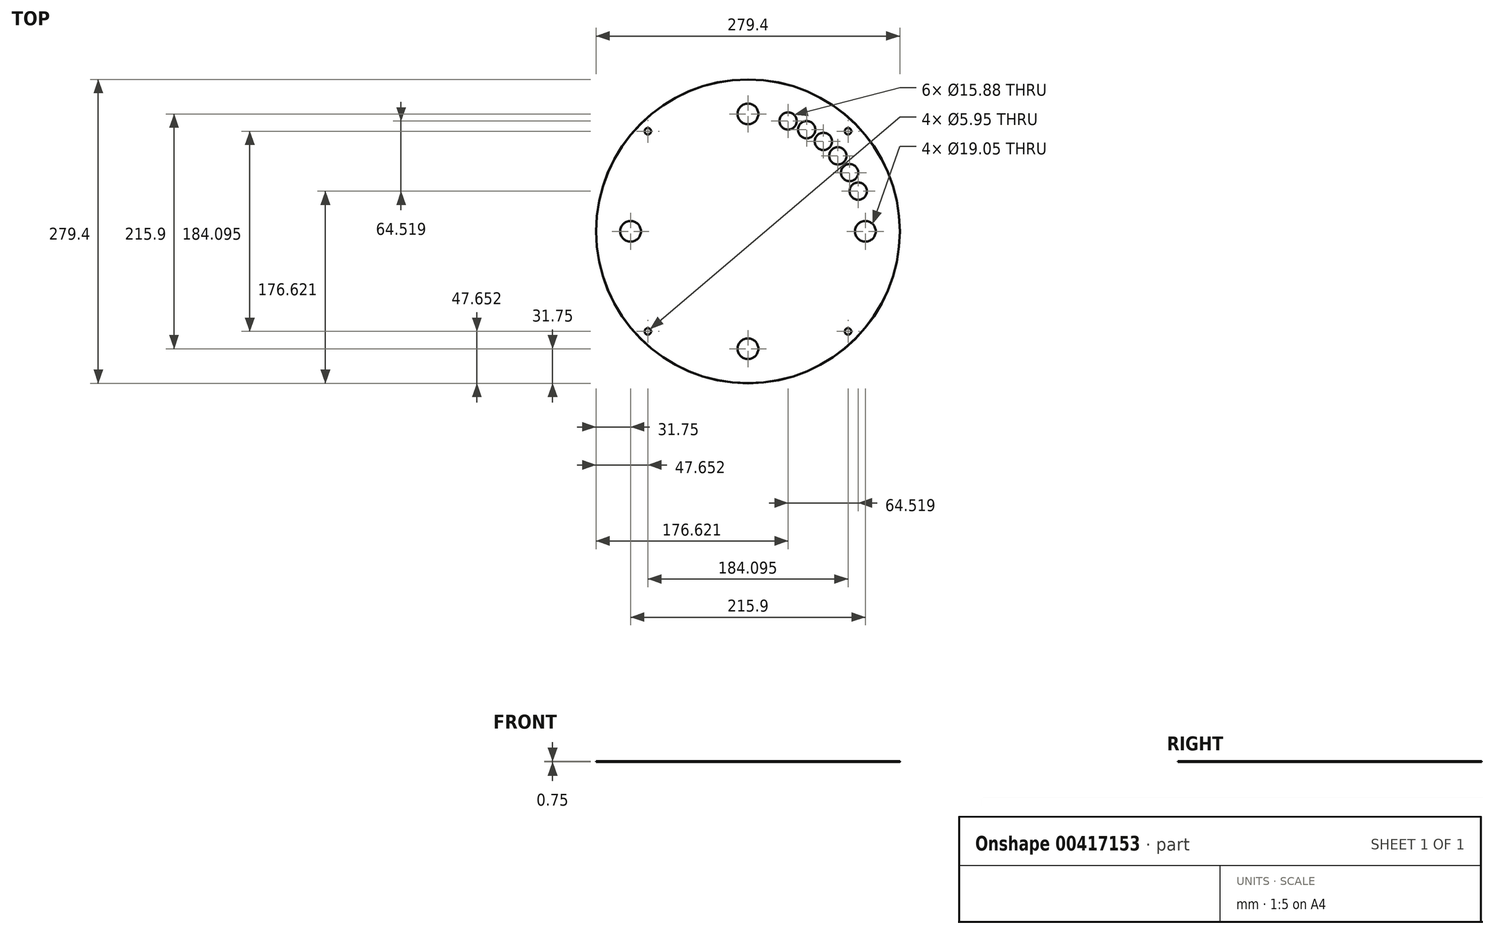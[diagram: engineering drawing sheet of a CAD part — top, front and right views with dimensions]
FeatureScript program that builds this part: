
annotation { "Feature Type Name" : "Feature", "Feature Type Description" : "" }
export const myFeature = defineFeature(function(context is Context, id is Id, definition is map)
    precondition{}
    {
        {
            assignVariable(context, id + "F0", {"name" : "BaseThickness", "anyValue" : 0.75});
        }
        {
            assignVariable(context, id + "F1", {"name" : "OuterChamfer", "anyValue" : 0.06});
        }
        {
            var Q0;
            Q0=qCreatedBy(makeId("Top.planeOp"),FACE);
            var sketch = newSketch(context, id + "F2", { "sketchPlane" : qUnion([Q0])});
            skCircle(sketch, "E0", {"center": v(0, 0) * mm, "radius": 139.7 * mm});
            skSolve(sketch);
        }
        {
            var Q0;
            Q0=qSketchRegion(id+"F2",true);
            extrude(context, id + "F3", {"entities" : qUnion([Q0]), "depth" : (getVariable(context, 'BaseThickness')) * mm});
        }
        {
            var Q0;
            Q0=makeQuery(id+"F3.opExtrude","CAP_EDGE",EDGE,{"disambiguationData":[OSD([sQuery(id+"F2.wireOp",EDGE,"E0")])],"isStart":false});
            var Q1;
            Q1=makeQuery(id+"F3.opExtrude","CAP_EDGE",EDGE,{"disambiguationData":[OSD([sQuery(id+"F2.wireOp",EDGE,"E0")])],"isStart":true});
            chamfer(context, id + "F4", {"entities" : qUnion([Q0, Q1]), "width" : (getVariable(context, 'OuterChamfer')) * mm, "tangentPropagation" : true});
        }
        {
            var Q0;
            Q0=makeQuery(id+"F3.opExtrude","CAP_FACE",FACE,{"disambiguationData":[OSD([sQuery(id+"F2.wireOp",EDGE,"E0")])],"isStart":false});
            var sketch = newSketch(context, id + "F5", { "sketchPlane" : qUnion([Q0])});
            skLineSegment(sketch, "E1", {"start": v(-215.84, 0) * mm, "end": v(221.7, 0) * mm, "construction": true});
            skLineSegment(sketch, "E2", {"start": v(0, 180) * mm, "end": v(0, -192.8) * mm, "construction": true});
            skLineSegment(sketch, "E3", {"start": v(0, 0) * mm, "end": v(159.36, -159.36) * mm, "construction": true});
            skCircle(sketch, "E4", {"center": v(0, 0) * mm, "radius": 130.18 * mm, "construction": true});
            skCircle(sketch, "E5", {"center": v(92.05, -92.05) * mm, "radius": 0.8 * mm});
            skCircle(sketch, "E6.1.0", {"center": v(-92.05, -92.05) * mm, "radius": 0.8 * mm});
            skCircle(sketch, "E6.2.0", {"center": v(-92.05, 92.05) * mm, "radius": 0.8 * mm});
            skCircle(sketch, "E6.3.0", {"center": v(92.05, 92.05) * mm, "radius": 0.8 * mm});
            skLineSegment(sketch, "E6.anchor1", {"start": v(0, 0) * mm, "end": v(92.05, -92.05) * mm, "construction": true});
            skLineSegment(sketch, "E6.anchor2", {"start": v(0, 0) * mm, "end": v(92.05, 92.05) * mm, "construction": true});
            skSolve(sketch);
        }
        {
            var Q0;
            Q0=makeQuery(id+"F5.imprint","IMPRINT",FACE,{"disambiguationData":[TD([[makeQuery(id+"F5.imprint","IMPRINT",EDGE,{"derivedFrom":sQuery(id+"F5.wireOp",EDGE,"E6.2.0")}),1.0]])]});
            var Q1;
            Q1=makeQuery(id+"F5.imprint","IMPRINT",FACE,{"disambiguationData":[TD([[makeQuery(id+"F5.imprint","IMPRINT",EDGE,{"derivedFrom":sQuery(id+"F5.wireOp",EDGE,"E6.3.0")}),1.0]])]});
            var Q2;
            Q2=makeQuery(id+"F5.imprint","IMPRINT",FACE,{"disambiguationData":[TD([[makeQuery(id+"F5.imprint","IMPRINT",EDGE,{"derivedFrom":sQuery(id+"F5.wireOp",EDGE,"E5")}),1.0]])]});
            var Q3;
            Q3=makeQuery(id+"F5.imprint","IMPRINT",FACE,{"disambiguationData":[TD([[makeQuery(id+"F5.imprint","IMPRINT",EDGE,{"derivedFrom":sQuery(id+"F5.wireOp",EDGE,"E6.1.0")}),1.0]])]});
            extrude(context, id + "F6", {"entities" : qUnion([Q0, Q1, Q2, Q3]), "operationType" : NewBodyOperationType.REMOVE, "endBound" : BoundingType.THROUGH_ALL, "oppositeDirection" : true, "depth" : 25.4 * mm});
        }
        {
            var Q0;
            Q0=makeQuery(id+"F3.opExtrude","CAP_FACE",FACE,{"disambiguationData":[OSD([sQuery(id+"F2.wireOp",EDGE,"E0")])],"isStart":false});
            var sketch = newSketch(context, id + "F7", { "sketchPlane" : qUnion([Q0])});
            skLineSegment(sketch, "E7", {"start": v(-165, 0) * mm, "end": v(189.59, 0) * mm, "construction": true});
            skLineSegment(sketch, "E8", {"start": v(0, 0) * mm, "end": v(123.83, -123.83) * mm, "construction": true});
            skCircle(sketch, "E9", {"center": v(0, 0) * mm, "radius": 130.18 * mm, "construction": true});
            skCircle(sketch, "E10", {"center": v(92.05, -92.05) * mm, "radius": 2.98 * mm});
            skCircle(sketch, "E11.1.0", {"center": v(92.05, 92.05) * mm, "radius": 2.98 * mm});
            skCircle(sketch, "E11.2.0", {"center": v(-92.05, 92.05) * mm, "radius": 2.98 * mm});
            skCircle(sketch, "E11.3.0", {"center": v(-92.05, -92.05) * mm, "radius": 2.98 * mm});
            skSolve(sketch);
        }
        {
            var Q0;
            Q0=makeQuery(id+"F7.imprint","IMPRINT",FACE,{"disambiguationData":[TD([[makeQuery(id+"F7.imprint","IMPRINT",EDGE,{"derivedFrom":sQuery(id+"F7.wireOp",EDGE,"E11.2.0")}),1.0]])]});
            var Q1;
            Q1=makeQuery(id+"F7.imprint","IMPRINT",FACE,{"disambiguationData":[TD([[makeQuery(id+"F7.imprint","IMPRINT",EDGE,{"derivedFrom":sQuery(id+"F7.wireOp",EDGE,"E11.1.0")}),1.0]])]});
            var Q2;
            Q2=makeQuery(id+"F7.imprint","IMPRINT",FACE,{"disambiguationData":[TD([[makeQuery(id+"F7.imprint","IMPRINT",EDGE,{"derivedFrom":sQuery(id+"F7.wireOp",EDGE,"E11.3.0")}),1.0]])]});
            var Q3;
            Q3=makeQuery(id+"F7.imprint","IMPRINT",FACE,{"disambiguationData":[TD([[makeQuery(id+"F7.imprint","IMPRINT",EDGE,{"derivedFrom":sQuery(id+"F7.wireOp",EDGE,"E10")}),1.0]])]});
            extrude(context, id + "F8", {"entities" : qUnion([Q0, Q1, Q2, Q3]), "operationType" : NewBodyOperationType.REMOVE, "endBound" : BoundingType.THROUGH_ALL, "oppositeDirection" : true, "depth" : 25.4 * mm});
        }
        {
            var Q0;
            Q0=makeQuery(id+"F3.opExtrude","CAP_FACE",FACE,{"disambiguationData":[OSD([sQuery(id+"F2.wireOp",EDGE,"E0")])],"isStart":false});
            var sketch = newSketch(context, id + "F9", { "sketchPlane" : qUnion([Q0])});
            skLineSegment(sketch, "E12", {"start": v(-167.71, 0) * mm, "end": v(197.5, 0) * mm, "construction": true});
            skLineSegment(sketch, "E13", {"start": v(197.5, 0) * mm, "end": v(197.5, -2.16) * mm, "construction": true});
            skCircle(sketch, "E14", {"center": v(0, 0) * mm, "radius": 107.95 * mm, "construction": true});
            skCircle(sketch, "E15", {"center": v(107.95, 0) * mm, "radius": 2.98 * mm});
            skCircle(sketch, "E16.1.0", {"center": v(0, 107.95) * mm, "radius": 2.98 * mm});
            skCircle(sketch, "E16.2.0", {"center": v(-107.95, 0) * mm, "radius": 2.98 * mm});
            skCircle(sketch, "E16.3.0", {"center": v(0, -107.95) * mm, "radius": 2.98 * mm});
            skSolve(sketch);
        }
        {
            var Q0;
            Q0=makeQuery(id+"F9.imprint","IMPRINT",FACE,{"disambiguationData":[TD([[makeQuery(id+"F9.imprint","IMPRINT",EDGE,{"derivedFrom":sQuery(id+"F9.wireOp",EDGE,"E16.1.0")}),1.0]])]});
            var Q1;
            Q1=makeQuery(id+"F9.imprint","IMPRINT",FACE,{"disambiguationData":[TD([[makeQuery(id+"F9.imprint","IMPRINT",EDGE,{"derivedFrom":sQuery(id+"F9.wireOp",EDGE,"E15")}),1.0]])]});
            var Q2;
            Q2=makeQuery(id+"F9.imprint","IMPRINT",FACE,{"disambiguationData":[TD([[makeQuery(id+"F9.imprint","IMPRINT",EDGE,{"derivedFrom":sQuery(id+"F9.wireOp",EDGE,"E16.3.0")}),1.0]])]});
            var Q3;
            Q3=makeQuery(id+"F9.imprint","IMPRINT",FACE,{"disambiguationData":[TD([[makeQuery(id+"F9.imprint","IMPRINT",EDGE,{"derivedFrom":sQuery(id+"F9.wireOp",EDGE,"E16.2.0")}),1.0]])]});
            extrude(context, id + "F10", {"entities" : qUnion([Q0, Q1, Q2, Q3]), "operationType" : NewBodyOperationType.REMOVE, "endBound" : BoundingType.THROUGH_ALL, "oppositeDirection" : true, "depth" : 25.4 * mm});
        }
        {
            var Q0;
            Q0=makeQuery(id+"F3.opExtrude","CAP_FACE",FACE,{"disambiguationData":[OSD([sQuery(id+"F2.wireOp",EDGE,"E0")])],"isStart":false});
            var sketch = newSketch(context, id + "F11", { "sketchPlane" : qUnion([Q0])});
            skLineSegment(sketch, "E17", {"start": v(-162.26, 0) * mm, "end": v(185.44, 0) * mm, "construction": true});
            skCircle(sketch, "E18", {"center": v(0, 0) * mm, "radius": 107.95 * mm, "construction": true});
            skCircle(sketch, "E19", {"center": v(107.95, 0) * mm, "radius": 9.53 * mm});
            skCircle(sketch, "E20.1.0", {"center": v(0, 107.95) * mm, "radius": 9.53 * mm});
            skCircle(sketch, "E20.2.0", {"center": v(-107.95, 0) * mm, "radius": 9.53 * mm});
            skCircle(sketch, "E20.3.0", {"center": v(0, -107.95) * mm, "radius": 9.53 * mm});
            skSolve(sketch);
        }
        {
            var Q0;
            Q0=makeQuery(id+"F11.imprint","IMPRINT",FACE,{"disambiguationData":[TD([[makeQuery(id+"F11.imprint","IMPRINT",EDGE,{"derivedFrom":sQuery(id+"F11.wireOp",EDGE,"E20.1.0")}),1.0]])]});
            var Q1;
            Q1=makeQuery(id+"F11.imprint","IMPRINT",FACE,{"disambiguationData":[TD([[makeQuery(id+"F11.imprint","IMPRINT",EDGE,{"derivedFrom":sQuery(id+"F11.wireOp",EDGE,"E19")}),1.0]])]});
            var Q2;
            Q2=makeQuery(id+"F11.imprint","IMPRINT",FACE,{"disambiguationData":[TD([[makeQuery(id+"F11.imprint","IMPRINT",EDGE,{"derivedFrom":sQuery(id+"F11.wireOp",EDGE,"E20.3.0")}),1.0]])]});
            var Q3;
            Q3=makeQuery(id+"F11.imprint","IMPRINT",FACE,{"disambiguationData":[TD([[makeQuery(id+"F11.imprint","IMPRINT",EDGE,{"derivedFrom":sQuery(id+"F11.wireOp",EDGE,"E20.2.0")}),1.0]])]});
            extrude(context, id + "F12", {"entities" : qUnion([Q0, Q1, Q2, Q3]), "operationType" : NewBodyOperationType.REMOVE, "oppositeDirection" : true, "depth" : 6.35 * mm});
        }
        {
            var Q0;
            Q0=makeQuery(id+"F3.opExtrude","CAP_FACE",FACE,{"disambiguationData":[OSD([sQuery(id+"F2.wireOp",EDGE,"E0")])],"isStart":false});
            var sketch = newSketch(context, id + "F13", { "sketchPlane" : qUnion([Q0])});
            skLineSegment(sketch, "E21", {"start": v(-158.85, 0) * mm, "end": v(169.45, 0) * mm, "construction": true});
            skCircle(sketch, "E22", {"center": v(0, 0) * mm, "radius": 107.95 * mm, "construction": true});
            skLineSegment(sketch, "E23", {"start": v(0, 0) * mm, "end": v(56.99, 156.57) * mm, "construction": true});
            skCircle(sketch, "E24", {"center": v(36.92, 101.44) * mm, "radius": 3.18 * mm});
            skCircle(sketch, "E25.1.0", {"center": v(53.97, 93.49) * mm, "radius": 3.18 * mm});
            skCircle(sketch, "E25.2.0", {"center": v(69.39, 82.7) * mm, "radius": 3.18 * mm});
            skCircle(sketch, "E25.3.0", {"center": v(82.7, 69.39) * mm, "radius": 3.18 * mm});
            skCircle(sketch, "E25.4.0", {"center": v(93.49, 53.98) * mm, "radius": 3.18 * mm});
            skCircle(sketch, "E25.5.0", {"center": v(101.44, 36.92) * mm, "radius": 3.18 * mm});
            skLineSegment(sketch, "E25.anchor1", {"start": v(0, 0) * mm, "end": v(36.92, 101.44) * mm, "construction": true});
            skLineSegment(sketch, "E25.anchor2", {"start": v(0, 0) * mm, "end": v(101.44, 36.92) * mm, "construction": true});
            skSolve(sketch);
        }
        {
            var Q0;
            Q0=makeQuery(id+"F13.imprint","IMPRINT",FACE,{"disambiguationData":[TD([[makeQuery(id+"F13.imprint","IMPRINT",EDGE,{"derivedFrom":sQuery(id+"F13.wireOp",EDGE,"E24")}),1.0]])]});
            var Q1;
            Q1=makeQuery(id+"F13.imprint","IMPRINT",FACE,{"disambiguationData":[TD([[makeQuery(id+"F13.imprint","IMPRINT",EDGE,{"derivedFrom":sQuery(id+"F13.wireOp",EDGE,"E25.1.0")}),1.0]])]});
            var Q2;
            Q2=makeQuery(id+"F13.imprint","IMPRINT",FACE,{"disambiguationData":[TD([[makeQuery(id+"F13.imprint","IMPRINT",EDGE,{"derivedFrom":sQuery(id+"F13.wireOp",EDGE,"E25.2.0")}),1.0]])]});
            var Q3;
            Q3=makeQuery(id+"F13.imprint","IMPRINT",FACE,{"disambiguationData":[TD([[makeQuery(id+"F13.imprint","IMPRINT",EDGE,{"derivedFrom":sQuery(id+"F13.wireOp",EDGE,"E25.3.0")}),1.0]])]});
            var Q4;
            Q4=makeQuery(id+"F13.imprint","IMPRINT",FACE,{"disambiguationData":[TD([[makeQuery(id+"F13.imprint","IMPRINT",EDGE,{"derivedFrom":sQuery(id+"F13.wireOp",EDGE,"E25.4.0")}),1.0]])]});
            var Q5;
            Q5=makeQuery(id+"F13.imprint","IMPRINT",FACE,{"disambiguationData":[TD([[makeQuery(id+"F13.imprint","IMPRINT",EDGE,{"derivedFrom":sQuery(id+"F13.wireOp",EDGE,"E25.5.0")}),1.0]])]});
            extrude(context, id + "F14", {"entities" : qUnion([Q0, Q1, Q2, Q3, Q4, Q5]), "operationType" : NewBodyOperationType.REMOVE, "endBound" : BoundingType.THROUGH_ALL, "oppositeDirection" : true, "depth" : 25.4 * mm});
        }
        {
            var Q0;
            Q0=makeQuery(id+"F3.opExtrude","CAP_FACE",FACE,{"disambiguationData":[OSD([sQuery(id+"F2.wireOp",EDGE,"E0")])],"isStart":true});
            var sketch = newSketch(context, id + "F15", { "sketchPlane" : qUnion([Q0])});
            skLineSegment(sketch, "E26", {"start": v(-162.24, 0) * mm, "end": v(180.02, 0) * mm, "construction": true});
            skLineSegment(sketch, "E27", {"start": v(0, 0) * mm, "end": v(173.64, -63.2) * mm, "construction": true});
            skCircle(sketch, "E28", {"center": v(0, 0) * mm, "radius": 101.85 * mm, "construction": true});
            skCircle(sketch, "E29", {"center": v(95.71, -34.84) * mm, "radius": 1.2 * mm});
            skCircle(sketch, "E30.1.0", {"center": v(88.2, -50.93) * mm, "radius": 1.2 * mm});
            skCircle(sketch, "E30.2.0", {"center": v(78.02, -65.47) * mm, "radius": 1.2 * mm});
            skCircle(sketch, "E30.3.0", {"center": v(65.47, -78.02) * mm, "radius": 1.2 * mm});
            skCircle(sketch, "E30.4.0", {"center": v(50.93, -88.2) * mm, "radius": 1.2 * mm});
            skLineSegment(sketch, "E30.anchor1", {"start": v(0, 0) * mm, "end": v(95.71, -34.84) * mm, "construction": true});
            skLineSegment(sketch, "E30.anchor2", {"start": v(0, 0) * mm, "end": v(34.84, -95.71) * mm, "construction": true});
            skCircle(sketch, "E31.1.5.0", {"center": v(34.84, -95.71) * mm, "radius": 1.2 * mm});
            skSolve(sketch);
        }
        {
            var Q0;
            Q0=makeQuery(id+"F15.imprint","IMPRINT",FACE,{"disambiguationData":[TD([[makeQuery(id+"F15.imprint","IMPRINT",EDGE,{"derivedFrom":sQuery(id+"F15.wireOp",EDGE,"E30.4.0")}),1.0]])]});
            var Q1;
            Q1=makeQuery(id+"F15.imprint","IMPRINT",FACE,{"disambiguationData":[TD([[makeQuery(id+"F15.imprint","IMPRINT",EDGE,{"derivedFrom":sQuery(id+"F15.wireOp",EDGE,"E30.3.0")}),1.0]])]});
            var Q2;
            Q2=makeQuery(id+"F15.imprint","IMPRINT",FACE,{"disambiguationData":[TD([[makeQuery(id+"F15.imprint","IMPRINT",EDGE,{"derivedFrom":sQuery(id+"F15.wireOp",EDGE,"E30.2.0")}),1.0]])]});
            var Q3;
            Q3=makeQuery(id+"F15.imprint","IMPRINT",FACE,{"disambiguationData":[TD([[makeQuery(id+"F15.imprint","IMPRINT",EDGE,{"derivedFrom":sQuery(id+"F15.wireOp",EDGE,"E30.1.0")}),1.0]])]});
            var Q4;
            Q4=makeQuery(id+"F15.imprint","IMPRINT",FACE,{"disambiguationData":[TD([[makeQuery(id+"F15.imprint","IMPRINT",EDGE,{"derivedFrom":sQuery(id+"F15.wireOp",EDGE,"E29")}),1.0]])]});
            var Q5;
            Q5=makeQuery(id+"F15.imprint","IMPRINT",FACE,{"disambiguationData":[TD([[makeQuery(id+"F15.imprint","IMPRINT",EDGE,{"derivedFrom":sQuery(id+"F15.wireOp",EDGE,"E31.1.5.0")}),1.0]])]});
            extrude(context, id + "F16", {"entities" : qUnion([Q0, Q1, Q2, Q3, Q4, Q5]), "operationType" : NewBodyOperationType.REMOVE, "oppositeDirection" : true, "depth" : 12.7 * mm});
        }
        {
            var Q0;
            Q0=makeQuery(id+"F3.opExtrude","CAP_FACE",FACE,{"disambiguationData":[OSD([sQuery(id+"F2.wireOp",EDGE,"E0")])],"isStart":true});
            var sketch = newSketch(context, id + "F17", { "sketchPlane" : qUnion([Q0])});
            skLineSegment(sketch, "E32", {"start": v(-158.6, 0) * mm, "end": v(161.84, 0) * mm, "construction": true});
            skLineSegment(sketch, "E33", {"start": v(0, 0) * mm, "end": v(151.3, -55.07) * mm, "construction": true});
            skCircle(sketch, "E34", {"center": v(0, 0) * mm, "radius": 107.95 * mm, "construction": true});
            skCircle(sketch, "E35", {"center": v(101.44, -36.92) * mm, "radius": 7.94 * mm});
            skCircle(sketch, "E36.1.0", {"center": v(93.49, -53.98) * mm, "radius": 7.94 * mm});
            skCircle(sketch, "E36.2.0", {"center": v(82.7, -69.39) * mm, "radius": 7.94 * mm});
            skCircle(sketch, "E36.3.0", {"center": v(69.39, -82.7) * mm, "radius": 7.94 * mm});
            skCircle(sketch, "E36.4.0", {"center": v(53.97, -93.49) * mm, "radius": 7.94 * mm});
            skCircle(sketch, "E36.5.0", {"center": v(36.92, -101.44) * mm, "radius": 7.94 * mm});
            skLineSegment(sketch, "E36.anchor1", {"start": v(0, 0) * mm, "end": v(101.44, -36.92) * mm, "construction": true});
            skLineSegment(sketch, "E36.anchor2", {"start": v(0, 0) * mm, "end": v(36.92, -101.44) * mm, "construction": true});
            skSolve(sketch);
        }
        {
            var Q0;
            Q0=makeQuery(id+"F17.imprint","IMPRINT",FACE,{"disambiguationData":[TD([[makeQuery(id+"F17.imprint","IMPRINT",EDGE,{"derivedFrom":sQuery(id+"F17.wireOp",EDGE,"E36.5.0")}),1.0]])]});
            var Q1;
            Q1=makeQuery(id+"F17.imprint","IMPRINT",FACE,{"disambiguationData":[TD([[makeQuery(id+"F17.imprint","IMPRINT",EDGE,{"derivedFrom":sQuery(id+"F17.wireOp",EDGE,"E36.4.0")}),1.0]])]});
            var Q2;
            Q2=makeQuery(id+"F17.imprint","IMPRINT",FACE,{"disambiguationData":[TD([[makeQuery(id+"F17.imprint","IMPRINT",EDGE,{"derivedFrom":sQuery(id+"F17.wireOp",EDGE,"E36.3.0")}),1.0]])]});
            var Q3;
            Q3=makeQuery(id+"F17.imprint","IMPRINT",FACE,{"disambiguationData":[TD([[makeQuery(id+"F17.imprint","IMPRINT",EDGE,{"derivedFrom":sQuery(id+"F17.wireOp",EDGE,"E36.2.0")}),1.0]])]});
            var Q4;
            Q4=makeQuery(id+"F17.imprint","IMPRINT",FACE,{"disambiguationData":[TD([[makeQuery(id+"F17.imprint","IMPRINT",EDGE,{"derivedFrom":sQuery(id+"F17.wireOp",EDGE,"E36.1.0")}),1.0]])]});
            var Q5;
            Q5=makeQuery(id+"F17.imprint","IMPRINT",FACE,{"disambiguationData":[TD([[makeQuery(id+"F17.imprint","IMPRINT",EDGE,{"derivedFrom":sQuery(id+"F17.wireOp",EDGE,"E35")}),1.0]])]});
            extrude(context, id + "F18", {"entities" : qUnion([Q0, Q1, Q2, Q3, Q4, Q5]), "operationType" : NewBodyOperationType.REMOVE, "oppositeDirection" : true, "depth" : 10.16 * mm});
        }
        {
            var Q0;
            Q0=makeQuery(id+"F3.opExtrude","CAP_FACE",FACE,{"disambiguationData":[OSD([sQuery(id+"F2.wireOp",EDGE,"E0")])],"isStart":false});
            var sketch = newSketch(context, id + "F19", { "sketchPlane" : qUnion([Q0])});
            skLineSegment(sketch, "E37", {"start": v(-156.56, 0) * mm, "end": v(178.38, 0) * mm, "construction": true});
            skLineSegment(sketch, "E38", {"start": v(0, 0) * mm, "end": v(51.83, 142.4) * mm, "construction": true});
            skCircle(sketch, "E39", {"center": v(0, 0) * mm, "radius": 107.95 * mm, "construction": true});
            skCircle(sketch, "E40", {"center": v(36.92, 101.44) * mm, "radius": 4.76 * mm});
            skCircle(sketch, "E41.1.0", {"center": v(53.97, 93.49) * mm, "radius": 4.76 * mm});
            skCircle(sketch, "E41.2.0", {"center": v(69.39, 82.7) * mm, "radius": 4.76 * mm});
            skCircle(sketch, "E41.3.0", {"center": v(82.7, 69.39) * mm, "radius": 4.76 * mm});
            skCircle(sketch, "E41.4.0", {"center": v(93.49, 53.98) * mm, "radius": 4.76 * mm});
            skCircle(sketch, "E41.5.0", {"center": v(101.44, 36.92) * mm, "radius": 4.76 * mm});
            skLineSegment(sketch, "E41.anchor1", {"start": v(0, 0) * mm, "end": v(36.92, 101.44) * mm, "construction": true});
            skLineSegment(sketch, "E41.anchor2", {"start": v(0, 0) * mm, "end": v(101.44, 36.92) * mm, "construction": true});
            skSolve(sketch);
        }
        {
            var Q0;
            Q0=makeQuery(id+"F19.imprint","IMPRINT",FACE,{"disambiguationData":[TD([[makeQuery(id+"F19.imprint","IMPRINT",EDGE,{"derivedFrom":sQuery(id+"F19.wireOp",EDGE,"E40")}),1.0]])]});
            var Q1;
            Q1=makeQuery(id+"F19.imprint","IMPRINT",FACE,{"disambiguationData":[TD([[makeQuery(id+"F19.imprint","IMPRINT",EDGE,{"derivedFrom":sQuery(id+"F19.wireOp",EDGE,"E41.1.0")}),1.0]])]});
            var Q2;
            Q2=makeQuery(id+"F19.imprint","IMPRINT",FACE,{"disambiguationData":[TD([[makeQuery(id+"F19.imprint","IMPRINT",EDGE,{"derivedFrom":sQuery(id+"F19.wireOp",EDGE,"E41.2.0")}),1.0]])]});
            var Q3;
            Q3=makeQuery(id+"F19.imprint","IMPRINT",FACE,{"disambiguationData":[TD([[makeQuery(id+"F19.imprint","IMPRINT",EDGE,{"derivedFrom":sQuery(id+"F19.wireOp",EDGE,"E41.3.0")}),1.0]])]});
            var Q4;
            Q4=makeQuery(id+"F19.imprint","IMPRINT",FACE,{"disambiguationData":[TD([[makeQuery(id+"F19.imprint","IMPRINT",EDGE,{"derivedFrom":sQuery(id+"F19.wireOp",EDGE,"E41.4.0")}),1.0]])]});
            var Q5;
            Q5=makeQuery(id+"F19.imprint","IMPRINT",FACE,{"disambiguationData":[TD([[makeQuery(id+"F19.imprint","IMPRINT",EDGE,{"derivedFrom":sQuery(id+"F19.wireOp",EDGE,"E41.5.0")}),1.0]])]});
            extrude(context, id + "F20", {"entities" : qUnion([Q0, Q1, Q2, Q3, Q4, Q5]), "operationType" : NewBodyOperationType.REMOVE, "oppositeDirection" : true, "depth" : 4.78 * mm});
        }
    });
